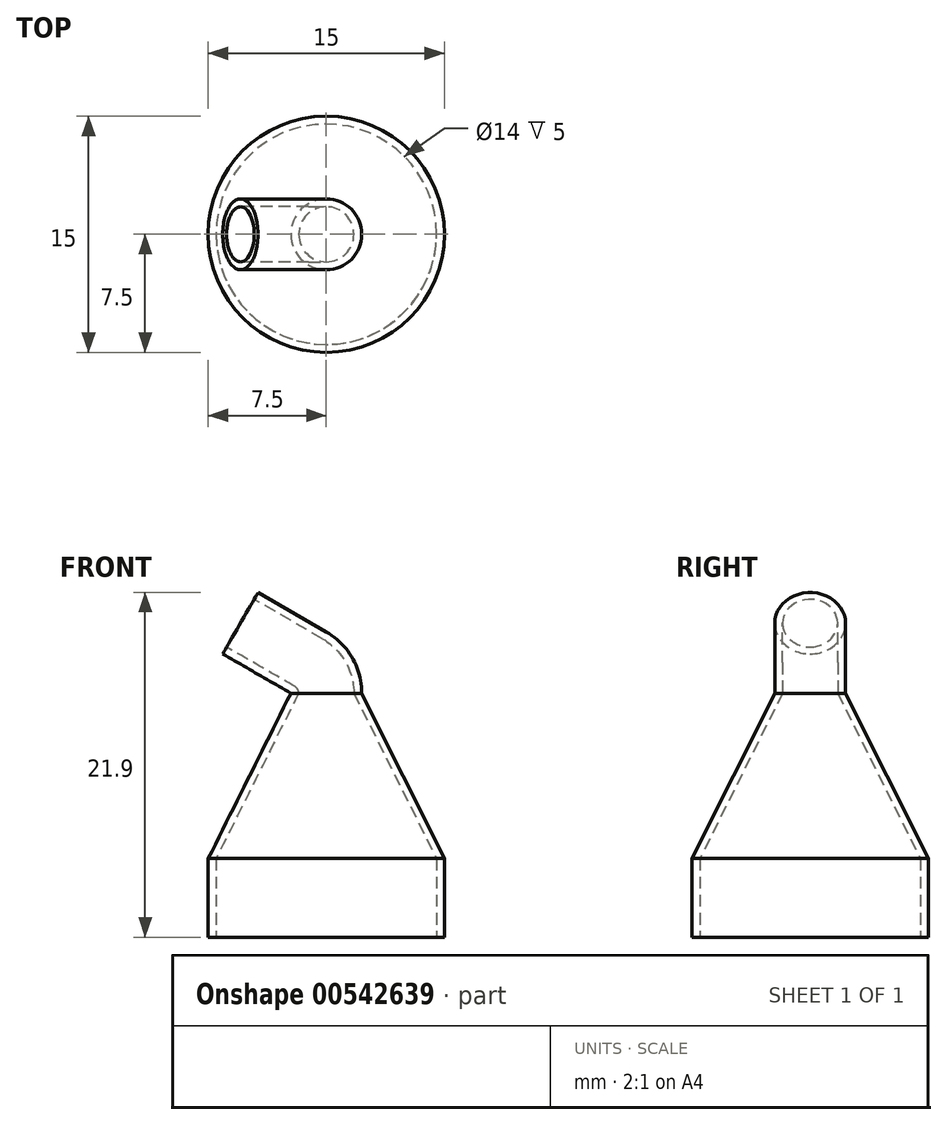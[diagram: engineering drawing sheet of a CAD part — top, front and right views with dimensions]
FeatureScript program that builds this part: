
annotation { "Feature Type Name" : "Feature", "Feature Type Description" : "" }
export const myFeature = defineFeature(function(context is Context, id is Id, definition is map)
    precondition{}
    {
        {
            var Q0;
            Q0=qCreatedBy(makeId("Top.planeOp"),FACE);
            var sketch = newSketch(context, id + "F0", { "sketchPlane" : qUnion([Q0])});
            skCircle(sketch, "E0", {"center": v(0, 0) * mm, "radius": 7.5 * mm});
            skCircle(sketch, "E1", {"center": v(0, 0) * mm, "radius": 7 * mm});
            skSolve(sketch);
        }
        {
            var Q0;
            Q0=makeQuery(id+"F0.imprint","IMPRINT",FACE,{"disambiguationData":[TD([[makeQuery(id+"F0.imprint","IMPRINT",EDGE,{"derivedFrom":sQuery(id+"F0.wireOp",EDGE,"E0")}),1.0]])]});
            extrude(context, id + "F1", {"entities" : qUnion([Q0]), "depth" : 5 * mm, "offsetDistance" : 25 * mm});
        }
        {
            var Q0;
            Q0=makeQuery(id+"F1.opExtrude","CAP_FACE",FACE,{"disambiguationData":[OSD([sQuery(id+"F0.wireOp",EDGE,"E0"),sQuery(id+"F0.wireOp",EDGE,"E1")])],"isStart":false});
            var sketch = newSketch(context, id + "F2", { "sketchPlane" : qUnion([Q0])});
            skCircle(sketch, "E2", {"center": v(0, 0) * mm, "radius": 7.5 * mm});
            skCircle(sketch, "E3", {"center": v(0, 0) * mm, "radius": 7 * mm});
            skSolve(sketch);
        }
        {
            var Q0;
            Q0=qCreatedBy(makeId("Front.planeOp"),FACE);
            var sketch = newSketch(context, id + "F3", { "sketchPlane" : qUnion([Q0])});
            skLineSegment(sketch, "E4", {"start": v(0, 15.5) * mm, "end": v(0, 5) * mm, "construction": true});
            skLineSegment(sketch, "E5", {"start": v(-2.25, 15.5) * mm, "end": v(-7.5, 5) * mm});
            skLineSegment(sketch, "E6", {"start": v(0, 5) * mm, "end": v(-7.5, 5) * mm, "construction": true});
            skLineSegment(sketch, "E7", {"start": v(-7.5, 5) * mm, "end": v(-7, 5) * mm, "construction": true});
            skLineSegment(sketch, "E8", {"start": v(-7, 5) * mm, "end": v(-1.75, 15.5) * mm});
            skLineSegment(sketch, "E9", {"start": v(0, 15.5) * mm, "end": v(-2.25, 15.5) * mm, "construction": true});
            skPoint(sketch, "E10.orphan", {"position": v(0, 20) * mm});
            skLineSegment(sketch, "E11", {"start": v(-2.25, 15.5) * mm, "end": v(-1.75, 15.5) * mm});
            skLineSegment(sketch, "E12", {"start": v(-7.5, 5) * mm, "end": v(-7, 5) * mm});
            skSolve(sketch);
        }
        {
            var Q0;
            Q0=makeQuery(id+"F3.imprint","IMPRINT",FACE,{"disambiguationData":[TD([[makeQuery(id+"F3.imprint","IMPRINT",EDGE,{"derivedFrom":sQuery(id+"F3.wireOp",EDGE,"E5")}),1.0]])]});
            var Q1;
            Q1=sQuery(id+"F2.wireOp",EDGE,"E3");
            revolve(context, id + "F4", {"operationType" : NewBodyOperationType.ADD, "entities" : qUnion([Q0]), "axis" : qUnion([Q1]), "revolveType" : RevolveType.FULL});
        }
        {
            var Q0;
            Q0=qCreatedBy(makeId("Front.planeOp"),FACE);
            var sketch = newSketch(context, id + "F5", { "sketchPlane" : qUnion([Q0])});
            skArc(sketch, "E13", {"start": v(0, 15.5) * mm, "mid": v(-0.3, 16.62) * mm, "end": v(-1.13, 17.45) * mm});
            skLineSegment(sketch, "E14", {"start": v(-2.25, 15.5) * mm, "end": v(-2.25, 19.95) * mm, "construction": true});
            skLineSegment(sketch, "E15", {"start": v(-2.25, 15.5) * mm, "end": v(-1.13, 17.45) * mm, "construction": true});
            skLineSegment(sketch, "E16", {"start": v(-1.13, 17.45) * mm, "end": v(-5.46, 19.95) * mm});
            skSolve(sketch);
        }
        {
            var Q0;
            Q0=makeQuery(id+"F4.opRevolve","SWEPT_FACE",FACE,{"disambiguationData":[OSD([sQuery(id+"F3.wireOp",EDGE,"E11")])]});
            var Q1;
            Q1=sQuery(id+"F5.wireOp",EDGE,"E16");
            var Q2;
            Q2=sQuery(id+"F5.wireOp",EDGE,"E13");
            sweep(context, id + "F6", {"operationType" : NewBodyOperationType.ADD, "profiles" : qUnion([Q0]), "path" : qUnion([Q1, Q2])});
        }
    });
